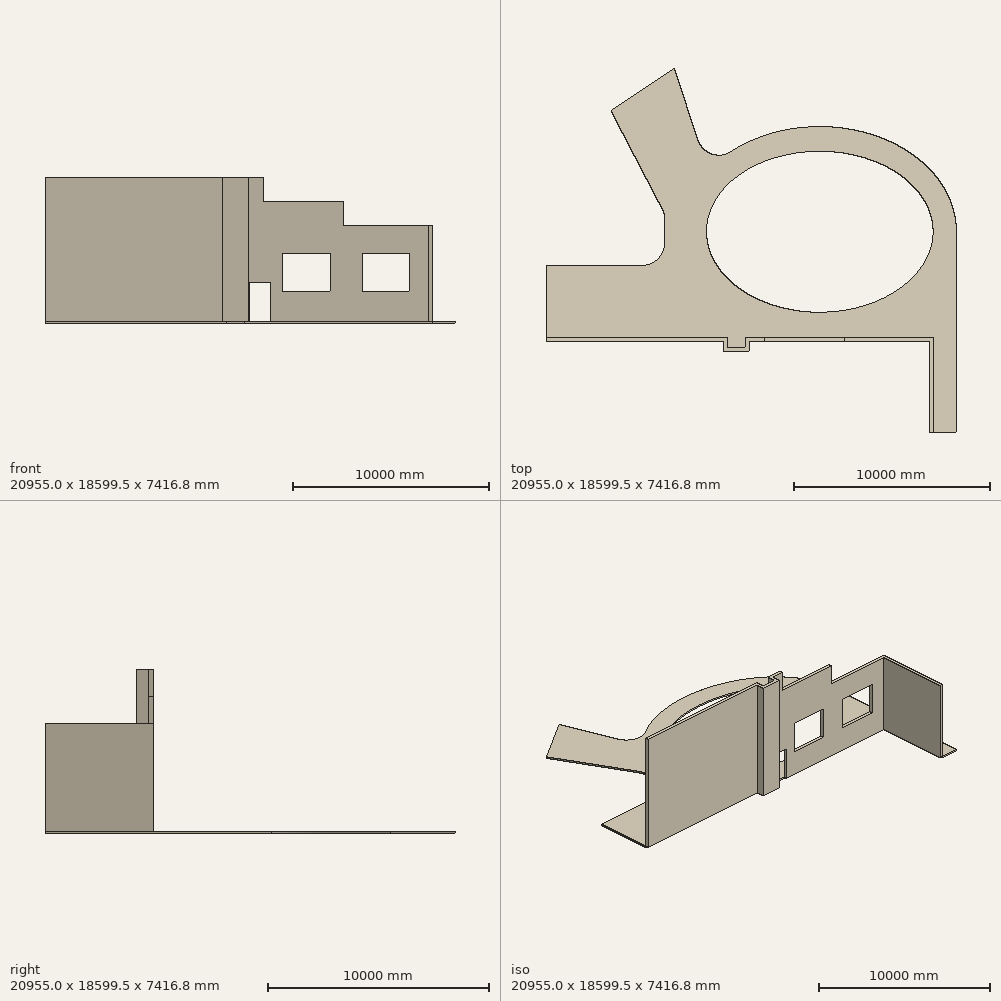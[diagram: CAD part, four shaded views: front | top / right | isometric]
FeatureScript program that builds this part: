
annotation { "Feature Type Name" : "Feature", "Feature Type Description" : "" }
export const myFeature = defineFeature(function(context is Context, id is Id, definition is map)
    precondition{}
    {
        {
            var Q0;
            Q0=qCreatedBy(makeId("Top.planeOp"),FACE);
            var sketch = newSketch(context, id + "F0", { "sketchPlane" : qUnion([Q0])});
            skEllipse(sketch, "E0", {"center": v(0, 0) * mm, "majorRadius": 5791.2 * mm, "minorRadius": 4114.8 * mm, "majorAxis": v(1, 0)});
            skLineSegment(sketch, "E1", {"start": v(6985, -10255.8) * mm, "end": v(6985, 0) * mm});
            skEllipticalArc(sketch, "E2", {});
            skLineSegment(sketch, "E3", {"start": v(6985, -10255.8) * mm, "end": v(5816.6, -10255.8) * mm});
            skLineSegment(sketch, "E4", {"start": v(5816.6, -10255.8) * mm, "end": v(5816.6, -5379) * mm});
            skLineSegment(sketch, "E5", {"start": v(5816.6, -5379) * mm, "end": v(-3810, -5379) * mm});
            skLineSegment(sketch, "E6", {"start": v(-3810, -5379) * mm, "end": v(-3810, -5912.4) * mm});
            skLineSegment(sketch, "E7", {"start": v(-3810, -5912.4) * mm, "end": v(-4724.4, -5912.4) * mm});
            skLineSegment(sketch, "E8", {"start": v(-4724.4, -5912.4) * mm, "end": v(-4724.4, -5379) * mm});
            skLineSegment(sketch, "E9", {"start": v(-4724.4, -5379) * mm, "end": v(-13970, -5379) * mm});
            skLineSegment(sketch, "E10", {"start": v(-13970, -5379) * mm, "end": v(-13970, -1721.4) * mm});
            skLineSegment(sketch, "E11", {"start": v(-13970, -1721.4) * mm, "end": v(-9067.8, -1721.4) * mm});
            skLineSegment(sketch, "E12", {"start": v(-7924.8, -578.4) * mm, "end": v(-7924.8, 627.78) * mm});
            skLineSegment(sketch, "E13", {"start": v(-8054.44, 1156.5) * mm, "end": v(-10676.8, 6182.52) * mm});
            skLineSegment(sketch, "E14", {"start": v(-10676.8, 6182.52) * mm, "end": v(-7440.06, 8343.69) * mm});
            skLineSegment(sketch, "E15", {"start": v(-7440.06, 8343.69) * mm, "end": v(-6233, 4696.9) * mm});
            skPoint(sketch, "E16.visualSharp", {"position": v(-5705.47, 3103.13) * mm});
            skArc(sketch, "E16.filletArc", {"start": v(-6233, 4696.9) * mm, "mid": v(-5524.68, 3976.96) * mm, "end": v(-4522.18, 4099.55) * mm});
            skPoint(sketch, "E17.visualSharp", {"position": v(-7924.8, 908.03) * mm});
            skArc(sketch, "E17.filletArc", {"start": v(-7924.8, 627.78) * mm, "mid": v(-7957.68, 899.97) * mm, "end": v(-8054.44, 1156.5) * mm});
            skPoint(sketch, "E18.visualSharp", {"position": v(-7924.8, -1721.4) * mm});
            skArc(sketch, "E18.filletArc", {"start": v(-9067.8, -1721.4) * mm, "mid": v(-8259.58, -1386.63) * mm, "end": v(-7924.8, -578.4) * mm});
            const initialGuessF0  = {"E2": [0, 0, 0, 1, 5.379007754885103, 6.985, 4.71238898038469, 0.7041856191442895]};
            skSetInitialGuess(sketch, initialGuessF0);
            skSolve(sketch);
        }
        {
            var Q0;
            Q0 = qSketchRegion(id + "F0", true);
            extrude(context, id + "F1", {"entities" : qUnion([Q0]), "oppositeDirection" : true, "depth" : 101.6 * mm, "offsetDistance" : 25.4 * mm});
        }
        {
            var Q0;
            Q0=qCreatedBy(makeId("Top.planeOp"),FACE);
            var sketch = newSketch(context, id + "F2", { "sketchPlane" : qUnion([Q0])});
            skLineSegment(sketch, "E19.0", {"start": v(5816.6, -10255.8) * mm, "end": v(5816.6, -5379) * mm});
            skLineSegment(sketch, "E20.0", {"start": v(5816.6, -5379) * mm, "end": v(-3810, -5379) * mm});
            skPoint(sketch, "E21.0", {"position": v(-3810, -5645.7) * mm});
            skLineSegment(sketch, "E22.0", {"start": v(-3810, -5912.4) * mm, "end": v(-4724.4, -5912.4) * mm});
            skLineSegment(sketch, "E23.0", {"start": v(-4724.4, -5912.4) * mm, "end": v(-4724.4, -5379) * mm});
            skLineSegment(sketch, "E24.0", {"start": v(-3810, -5379) * mm, "end": v(-3810, -5912.4) * mm});
            skLineSegment(sketch, "E25.0", {"start": v(-4724.4, -5379) * mm, "end": v(-13970, -5379) * mm});
            skLineSegment(sketch, "E26.0", {"start": v(-4927.6, -5582.2) * mm, "end": v(-13970, -5582.2) * mm});
            skLineSegment(sketch, "E26.1", {"start": v(-4927.6, -6115.6) * mm, "end": v(-4927.6, -5582.2) * mm});
            skLineSegment(sketch, "E26.2", {"start": v(5613.4, -10255.8) * mm, "end": v(5613.4, -5582.2) * mm});
            skLineSegment(sketch, "E26.3", {"start": v(5613.4, -5582.2) * mm, "end": v(-3606.8, -5582.2) * mm});
            skLineSegment(sketch, "E26.4", {"start": v(-3606.8, -5582.2) * mm, "end": v(-3606.8, -6115.6) * mm});
            skLineSegment(sketch, "E26.5", {"start": v(-3606.8, -6115.6) * mm, "end": v(-4927.6, -6115.6) * mm});
            skLineSegment(sketch, "E27", {"start": v(5613.4, -10255.8) * mm, "end": v(5816.6, -10255.8) * mm});
            skLineSegment(sketch, "E28", {"start": v(-13970, -5379) * mm, "end": v(-13970, -5582.2) * mm});
            skSolve(sketch);
        }
        {
            var Q0;
            Q0 = qSketchRegion(id + "F2", true);
            extrude(context, id + "F3", {"entities" : qUnion([Q0]), "depth" : 7315.2 * mm, "offsetDistance" : 25.4 * mm});
        }
        {
            var Q0;
            Q0=makeQuery(id+"F3.opExtrude","SWEPT_FACE",FACE,{"disambiguationData":[OSD([sQuery(id+"F2.wireOp",EDGE,"E20.0")])]});
            var sketch = newSketch(context, id + "F4", { "sketchPlane" : qUnion([Q0])});
            skLineSegment(sketch, "E29", {"start": v(-5816.6, 4876.8) * mm, "end": v(-1244.6, 4876.8) * mm});
            skLineSegment(sketch, "E30", {"start": v(-1244.6, 4876.8) * mm, "end": v(-1244.6, 6096) * mm});
            skLineSegment(sketch, "E31", {"start": v(-1244.6, 6096) * mm, "end": v(2819.4, 6096) * mm});
            skLineSegment(sketch, "E32", {"start": v(2819.4, 6096) * mm, "end": v(2819.4, 7315.2) * mm});
            skLineSegment(sketch, "E33", {"start": v(2819.4, 7315.2) * mm, "end": v(-5816.6, 7315.2) * mm});
            skLineSegment(sketch, "E34", {"start": v(-5816.6, 7315.2) * mm, "end": v(-5816.6, 4876.8) * mm});
            skLineSegment(sketch, "E35.bottom", {"start": v(-2209.8, 3454.4) * mm, "end": v(-4648.2, 3454.4) * mm});
            skLineSegment(sketch, "E35.top", {"start": v(-2209.8, 1524) * mm, "end": v(-4648.2, 1524) * mm});
            skLineSegment(sketch, "E35.left", {"start": v(-2209.8, 3454.4) * mm, "end": v(-2209.8, 1524) * mm});
            skLineSegment(sketch, "E35.right", {"start": v(-4648.2, 3454.4) * mm, "end": v(-4648.2, 1524) * mm});
            skPoint(sketch, "E35.middle", {"position": v(-3429, 2489.2) * mm});
            skLineSegment(sketch, "E36.bottom", {"start": v(1852.88, 3454.4) * mm, "end": v(-585.52, 3454.4) * mm});
            skLineSegment(sketch, "E36.top", {"start": v(1852.88, 1524) * mm, "end": v(-585.52, 1524) * mm});
            skLineSegment(sketch, "E36.left", {"start": v(1852.88, 3454.4) * mm, "end": v(1852.88, 1524) * mm});
            skLineSegment(sketch, "E36.right", {"start": v(-585.52, 3454.4) * mm, "end": v(-585.52, 1524) * mm});
            skPoint(sketch, "E36.middle", {"position": v(633.68, 2489.2) * mm});
            skLineSegment(sketch, "E37.bottom", {"start": v(2476.96, 0) * mm, "end": v(3543.76, 0) * mm});
            skLineSegment(sketch, "E37.top", {"start": v(2476.96, 1981.2) * mm, "end": v(3543.76, 1981.2) * mm});
            skLineSegment(sketch, "E37.left", {"start": v(2476.96, 0) * mm, "end": v(2476.96, 1981.2) * mm});
            skLineSegment(sketch, "E37.right", {"start": v(3543.76, 0) * mm, "end": v(3543.76, 1981.2) * mm});
            skPoint(sketch, "E37.middle", {"position": v(3010.36, 990.6) * mm});
            skSolve(sketch);
        }
        {
            var Q0;
            Q0 = qSketchRegion(id + "F4", true);
            extrude(context, id + "F5", {"entities" : qUnion([Q0]), "operationType" : NewBodyOperationType.REMOVE, "endBound" : BoundingType.THROUGH_ALL, "oppositeDirection" : true, "depth" : 25.4 * mm, "offsetDistance" : 25.4 * mm});
        }
    });
